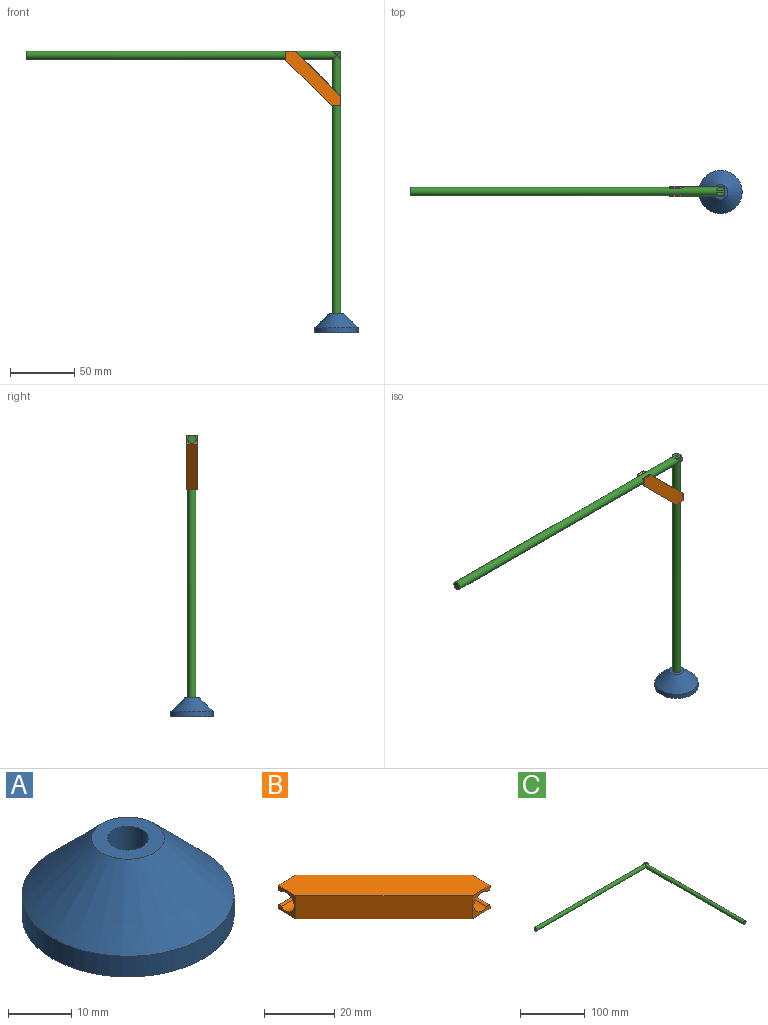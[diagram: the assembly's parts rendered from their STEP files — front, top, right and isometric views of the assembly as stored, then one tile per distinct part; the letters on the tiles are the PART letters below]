
ASSEMBLY  parts=3 mates=4
PART A: 5 faces, bbox 33.5x33.5x15 mm
  f0: cylinder r=3.25mm len=15mm, axis (0,0,-1), area 306.3mm2, adj f1,f4
  f1: plane 33.5x33.5mm, normal (0,0,-1), area 848.2mm2, adj f0,f2
  f2: cylinder r=16.75mm len=33.5mm, axis (0,0,-1), area 421mm2, adj f1,f3
  f3: cone r=16.75mm half-angle=45deg, axis (0,0,-1), area 1099.6mm2, adj f2,f4
  f4: plane 11.5x11.5mm, normal (0,0,1), area 70.7mm2, adj f0,f3
PART B: 16 faces, bbox 42.6x42.6x8 mm
  f0: plane 7.22x0.75mm, normal (1,0,0), area 5.4mm2, adj f3,f7,f9,f13
  f1: plane 7.22x0.75mm, normal (0,1,0), area 5.4mm2, adj f3,f5,f9,f14
  f2: plane 7.22x0.75mm, normal (1,0,0), area 5.4mm2, adj f3,f7,f8,f12
  f3: plane 35.36x35.36mm, normal (0.71,0.71,0), area 301mm2, adj f0,f1,f2,f4,f8,f9,f10,f11
  f4: plane 7.22x0.75mm, normal (0,1,0), area 5.4mm2, adj f3,f5,f8,f15
  f5: plane 8x7.22mm, normal (-1,0,0), area 22.8mm2, adj f1,f4,f6,f8,f9,f10,f14,f15
  f6: plane 35.36x35.36mm, normal (-0.71,-0.71,0), area 400mm2, adj f5,f7,f8,f9
  f7: plane 8x7.22mm, normal (0,-1,0), area 22.8mm2, adj f0,f2,f6,f8,f9,f11,f12,f13
  f8: plane 42.58x42.58mm, normal (0,0,1), area 562.7mm2, adj f2,f3,f4,f5,f6,f7
  f9: plane 42.58x42.58mm, normal (0,0,-1), area 562.7mm2, adj f0,f1,f3,f5,f6,f7
  f10: cylinder r=3.25mm len=13.71mm, axis (-1,0,0), area 167mm2, adj f3,f5,f14,f15
  f11: cylinder r=3.25mm len=13.71mm, axis (0,-1,0), area 167mm2, adj f3,f7,f12,f13
  f12: cylinder r=0.8mm len=8.5mm, axis (0,-1,0), area 13.7mm2, adj f2,f3,f7,f11
  f13: cylinder r=0.8mm len=8.5mm, axis (0,-1,0), area 13.7mm2, adj f0,f3,f7,f11
  f14: cylinder r=0.8mm len=8.5mm, axis (-1,0,0), area 13.7mm2, adj f1,f3,f5,f10
  f15: cylinder r=0.8mm len=8.5mm, axis (-1,0,0), area 13.7mm2, adj f3,f4,f5,f10
PART C: 14 faces, bbox 244.6x219.2x6.5 mm
  f0: cylinder r=3.25mm len=244.43mm, axis (1,0,0), area 4896.6mm2, adj f1,f2,f5,f10,f11,f12,f13
  f1: plane 1.79x0.13mm, normal (1,0,0), area 0.1mm2, adj f0,f3
  f2: plane 6.5x6.5mm, normal (-1,0,0), area 33.2mm2, adj f0
  f3: plane 1.79x0.13mm, normal (0,1,0), area 0.1mm2, adj f1,f5
  f4: plane 6.5x6.5mm, normal (0,-1,0), area 33.2mm2, adj f5
  f5: cylinder r=3.25mm len=219.03mm, axis (0,1,0), area 4378mm2, adj f0,f3,f4,f6,f7,f8,f9
  f6: plane 6.25x2.36mm, normal (1,0,0), area 10.9mm2, adj f5,f7
  f7: cylinder r=3.25mm len=6.25mm, axis (1,0,0), area 10.9mm2, adj f5,f6,f11
  f8: plane 6.25x2.36mm, normal (1,0,0), area 10.9mm2, adj f5,f9
  f9: cylinder r=3.25mm len=6.25mm, axis (1,0,0), area 10.9mm2, adj f5,f8,f12
  f10: plane 6.25x2.36mm, normal (0,1,0), area 10.9mm2, adj f0,f11
  f11: cylinder r=3.25mm len=6.25mm, axis (0,1,0), area 10.9mm2, adj f0,f7,f10
  f12: cylinder r=3.25mm len=6.25mm, axis (0,1,0), area 10.9mm2, adj f0,f9,f13
  f13: plane 6.25x2.36mm, normal (0,1,0), area 10.9mm2, adj f0,f12
PLACE A t=(116.99,-42.11,-106.1)mm
PLACE B rot(axis=(1,0,0),90deg) t=(98.93,-38.11,91.74)mm
PLACE C rot(axis=(1,0,0),90deg) t=(116.99,-42.11,109.8)mm
MATE cylindrical B.f11 <-> C.f5  axis (0,0,-1) through (116.99,-42.11,77.34)mm
MATE planar A.f0 <-> C.f5  axis (0,0,-1) through (116.99,-42.11,-106.1)mm
MATE cylindrical B.f10 <-> C.f0  axis (-1,0,0) through (84.52,-42.11,109.8)mm
MATE cylindrical C.f5 <-> A.f0  axis (0,0,1) through (116.99,-42.11,3.42)mm
